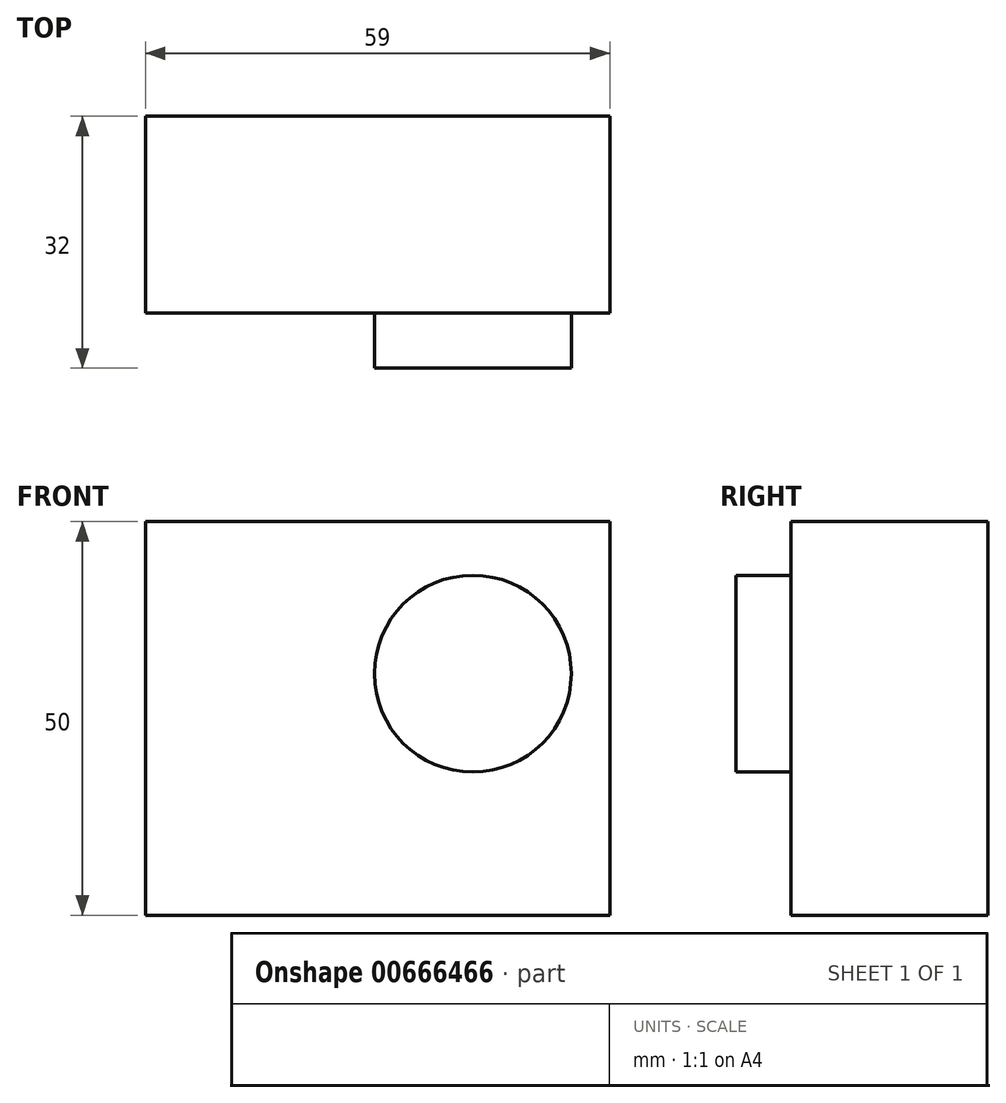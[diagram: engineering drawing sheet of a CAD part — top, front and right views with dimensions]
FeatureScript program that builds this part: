
annotation { "Feature Type Name" : "Feature", "Feature Type Description" : "" }
export const myFeature = defineFeature(function(context is Context, id is Id, definition is map)
    precondition{}
    {
        {
            var Q0;
            Q0=qCreatedBy(makeId("Front.planeOp"),FACE);
            var sketch = newSketch(context, id + "F0", { "sketchPlane" : qUnion([Q0])});
            skLineSegment(sketch, "E0.bottom", {"start": v(29.5, -25) * mm, "end": v(-29.5, -25) * mm});
            skLineSegment(sketch, "E0.top", {"start": v(29.5, 25) * mm, "end": v(-29.5, 25) * mm});
            skLineSegment(sketch, "E0.left", {"start": v(29.5, -25) * mm, "end": v(29.5, 25) * mm});
            skLineSegment(sketch, "E0.right", {"start": v(-29.5, -25) * mm, "end": v(-29.5, 25) * mm});
            skPoint(sketch, "E0.middle", {"position": v(0, 0) * mm});
            skSolve(sketch);
        }
        {
            var Q0;
            Q0 = qSketchRegion(id + "F0", true);
            extrude(context, id + "F1", {"entities" : qUnion([Q0]), "endBound" : BoundingType.SYMMETRIC, "depth" : 25 * mm, "offsetDistance" : 25 * mm});
        }
        {
            assignVariable(context, id + "F2", {"name" : "objectiveLength", "anyValue" : 7});
        }
        {
            var Q0;
            Q0=makeQuery(id+"F1.opExtrude","CAP_FACE",FACE,{"disambiguationData":[OSD([sQuery(id+"F0.wireOp",EDGE,"E0.bottom"),sQuery(id+"F0.wireOp",EDGE,"E0.top"),sQuery(id+"F0.wireOp",EDGE,"E0.left"),sQuery(id+"F0.wireOp",EDGE,"E0.right")])],"isStart":false});
            var sketch = newSketch(context, id + "F3", { "sketchPlane" : qUnion([Q0])});
            skCircle(sketch, "E1", {"center": v(12.1, 5.69) * mm, "radius": 12.5 * mm});
            skSolve(sketch);
        }
        {
            var Q0;
            Q0=makeQuery(id+"F3.imprint","IMPRINT",FACE,{"disambiguationData":[TD([[makeQuery(id+"F3.imprint","IMPRINT",EDGE,{"derivedFrom":sQuery(id+"F3.wireOp",EDGE,"E1")}),1.0]])]});
            extrude(context, id + "F4", {"entities" : qUnion([Q0]), "operationType" : NewBodyOperationType.ADD, "depth" : (getVariable(context, 'objectiveLength')) * mm, "offsetDistance" : 25 * mm});
        }
    });
